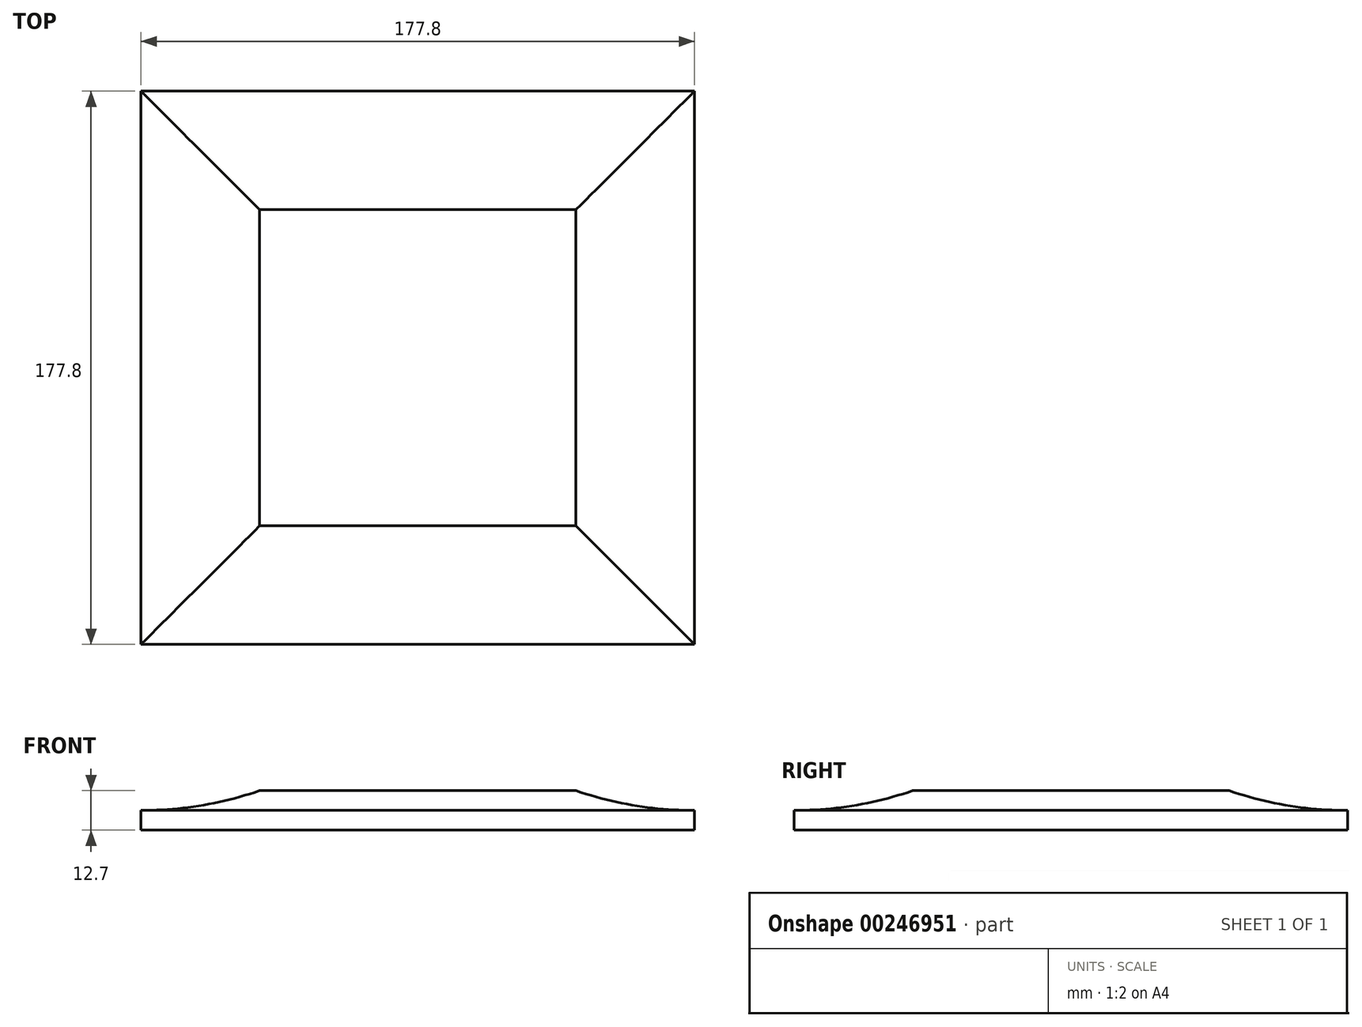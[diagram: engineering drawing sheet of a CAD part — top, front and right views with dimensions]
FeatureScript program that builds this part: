
annotation { "Feature Type Name" : "Feature", "Feature Type Description" : "" }
export const myFeature = defineFeature(function(context is Context, id is Id, definition is map)
    precondition{}
    {
        {
            var Q0;
            Q0=qCreatedBy(makeId("Top.planeOp"),FACE);
            var sketch = newSketch(context, id + "F0", { "sketchPlane" : qUnion([Q0])});
            skLineSegment(sketch, "E0.bottom", {"start": v(88.9, -88.9) * mm, "end": v(-88.9, -88.9) * mm});
            skLineSegment(sketch, "E0.top", {"start": v(88.9, 88.9) * mm, "end": v(-88.9, 88.9) * mm});
            skLineSegment(sketch, "E0.left", {"start": v(88.9, -88.9) * mm, "end": v(88.9, 88.9) * mm});
            skLineSegment(sketch, "E0.right", {"start": v(-88.9, -88.9) * mm, "end": v(-88.9, 88.9) * mm});
            skPoint(sketch, "E0.middle", {"position": v(0, 0) * mm});
            skSolve(sketch);
        }
        {
            var Q0;
            Q0=qCreatedBy(makeId("Front.planeOp"),FACE);
            var sketch = newSketch(context, id + "F1", { "sketchPlane" : qUnion([Q0])});
            skPoint(sketch, "E1.0", {"position": v(88.9, 0) * mm});
            skLineSegment(sketch, "E2", {"start": v(0, 0) * mm, "end": v(88.9, 0) * mm});
            skLineSegment(sketch, "E3", {"start": v(88.9, 0) * mm, "end": v(88.9, 6.35) * mm});
            skLineSegment(sketch, "E4", {"start": v(88.9, 6.35) * mm, "end": v(106.7, 6.35) * mm, "construction": true});
            skLineSegment(sketch, "E5", {"start": v(0, 0) * mm, "end": v(0, 12.7) * mm});
            skLineSegment(sketch, "E6", {"start": v(0, 12.7) * mm, "end": v(50.8, 12.7) * mm});
            skArc(sketch, "E7", {"start": v(88.9, 6.35) * mm, "mid": v(69.59, 7.95) * mm, "end": v(50.8, 12.7) * mm});
            skSolve(sketch);
        }
        {
            var Q0;
            Q0=makeQuery(id+"F1.imprint","IMPRINT",FACE,{"disambiguationData":[TD([[makeQuery(id+"F1.imprint","IMPRINT",EDGE,{"derivedFrom":sQuery(id+"F1.wireOp",EDGE,"E2")}),1.0]])]});
            var Q1;
            Q1 = qConstructionFilter(qBodyType(qCreatedBy(id + "F0" ,EDGE), BodyType.WIRE), ConstructionObject.NO);
            sweep(context, id + "F2", {"profiles" : qUnion([Q0]), "path" : qUnion([Q1])});
        }
    });
